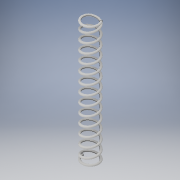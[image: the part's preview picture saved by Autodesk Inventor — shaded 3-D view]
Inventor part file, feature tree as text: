
AUTODESK INVENTOR PART (.ipt)
format: ipt  version: 2018 (Build 220112000, 112)  size: 387,584 bytes
history: native  units: in
note: dims shown in document units (in); Inventor stores cm internally (conversion verified against a paired STEP export)
features: helix x1, sketch x1
ambient origin geometry x8: Origin, YZ Plane, XZ Plane, XY Plane, X Axis, Y Axis, Z Axis, Center Point
bodies: Solid1 (feature_tree)
feature tree (2):
  helix  "Coil1"  [1 undecoded]
  sketch  "Sketch1"  dims[d1=0.0875in d2=1.0in d3=1.2in d4=5.1181in d5=0.0in d6=90.0deg d7=1.3743in d8=90.0deg d9=1.3743in]
note: 1 required parameter value undecoded (feature->parameter linkage not recoverable at this tier; creation-order binding heuristic only, values carry confidence <= 0.55)
